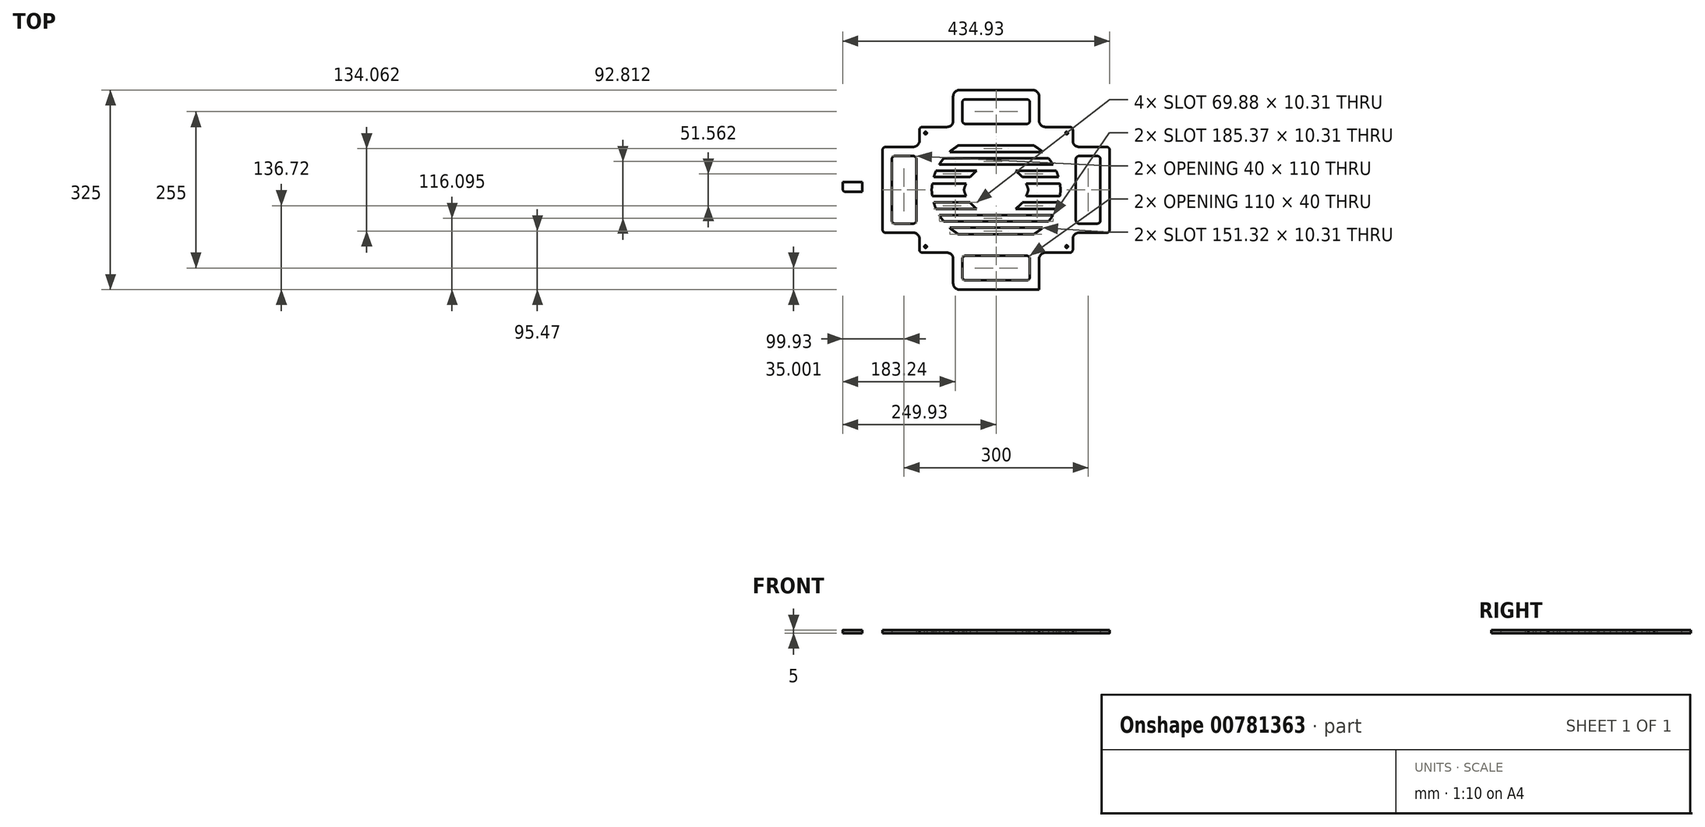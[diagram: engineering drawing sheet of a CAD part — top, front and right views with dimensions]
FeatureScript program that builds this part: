
annotation { "Feature Type Name" : "Feature", "Feature Type Description" : "" }
export const myFeature = defineFeature(function(context is Context, id is Id, definition is map)
    precondition{}
    {
        {
            var Q0;
            Q0=qCreatedBy(makeId("Top.planeOp"),FACE);
            var sketch = newSketch(context, id + "F0", { "sketchPlane" : qUnion([Q0])});
            skCircle(sketch, "E0", {"center": v(-230, 122.51) * mm, "radius": 2 * mm});
            skCircle(sketch, "E1", {"center": v(0, 122.51) * mm, "radius": 2 * mm});
            skCircle(sketch, "E2", {"center": v(0, -62.49) * mm, "radius": 2 * mm});
            skCircle(sketch, "E3", {"center": v(-230, -62.49) * mm, "radius": 2 * mm});
            skLineSegment(sketch, "E4.0", {"start": v(-230, 132.51) * mm, "end": v(-185, 132.51) * mm});
            skLineSegment(sketch, "E5.0", {"start": v(-240, 127.51) * mm, "end": v(-240, 110.01) * mm});
            skLineSegment(sketch, "E5.1", {"start": v(-235, 132.51) * mm, "end": v(-195, 132.51) * mm});
            skLineSegment(sketch, "E5.2", {"start": v(10, 127.51) * mm, "end": v(10, 110.01) * mm});
            skLineSegment(sketch, "E5.3", {"start": v(-235, -72.49) * mm, "end": v(-195, -72.49) * mm});
            skPoint(sketch, "E6.end.orphan", {"position": v(-290, 0) * mm});
            skLineSegment(sketch, "E7.bottom", {"start": v(-271.57, -39.99) * mm, "end": v(-290, -39.99) * mm});
            skPoint(sketch, "E8.end.orphan", {"position": v(-310, -39.99) * mm});
            skLineSegment(sketch, "E9", {"start": v(-290, 100.01) * mm, "end": v(-250, 100.01) * mm});
            skLineSegment(sketch, "E10", {"start": v(-290, -39.99) * mm, "end": v(-250, -39.99) * mm});
            skPoint(sketch, "E11.start.orphan", {"position": v(-240, 30.01) * mm});
            skLineSegment(sketch, "E12", {"start": v(-295, -39.99) * mm, "end": v(-290, -39.99) * mm});
            skLineSegment(sketch, "E13", {"start": v(-290, -39.99) * mm, "end": v(-295, -39.99) * mm});
            skLineSegment(sketch, "E14", {"start": v(-300, -34.99) * mm, "end": v(-300, 95.01) * mm});
            skLineSegment(sketch, "E15", {"start": v(-295, 100.01) * mm, "end": v(-290, 100.01) * mm});
            skPoint(sketch, "E16.visualSharp", {"position": v(-300, 100.01) * mm});
            skArc(sketch, "E16.filletArc", {"start": v(-295, 100.01) * mm, "mid": v(-298.54, 98.55) * mm, "end": v(-300, 95.01) * mm});
            skPoint(sketch, "E17.visualSharp", {"position": v(-300, -39.99) * mm});
            skArc(sketch, "E17.filletArc", {"start": v(-300, -34.99) * mm, "mid": v(-298.54, -38.52) * mm, "end": v(-295, -39.99) * mm});
            skLineSegment(sketch, "E18.0", {"start": v(-285, -19.99) * mm, "end": v(-285, 80.01) * mm});
            skLineSegment(sketch, "E19.0", {"start": v(-280, 85.01) * mm, "end": v(-250, 85.01) * mm});
            skLineSegment(sketch, "E20.0", {"start": v(-280, -24.99) * mm, "end": v(-250, -24.99) * mm});
            skPoint(sketch, "E21.visualSharp", {"position": v(-285, 85.01) * mm});
            skArc(sketch, "E21.filletArc", {"start": v(-280, 85.01) * mm, "mid": v(-283.54, 83.55) * mm, "end": v(-285, 80.01) * mm});
            skPoint(sketch, "E22.visualSharp", {"position": v(-285, -24.99) * mm});
            skArc(sketch, "E22.filletArc", {"start": v(-285, -19.99) * mm, "mid": v(-283.54, -23.52) * mm, "end": v(-280, -24.99) * mm});
            skLineSegment(sketch, "E23", {"start": v(-245, 68.7) * mm, "end": v(-245, 80.01) * mm});
            skLineSegment(sketch, "E24", {"start": v(-245, 80.01) * mm, "end": v(-245, -19.99) * mm});
            skArc(sketch, "E25.filletArc", {"start": v(-250, -24.99) * mm, "mid": v(-246.46, -23.52) * mm, "end": v(-245, -19.99) * mm});
            skArc(sketch, "E26.filletArc", {"start": v(-245, 80.01) * mm, "mid": v(-246.46, 83.55) * mm, "end": v(-250, 85.01) * mm});
            skLineSegment(sketch, "E27", {"start": v(-361.14, -2.55) * mm, "end": v(-350.49, -2.55) * mm});
            skLineSegment(sketch, "E28", {"start": v(-340.49, -12.55) * mm, "end": v(-340.49, -26.99) * mm});
            skPoint(sketch, "E29.visualSharp", {"position": v(-340.49, -2.55) * mm});
            skArc(sketch, "E29.filletArc", {"start": v(-340.49, -12.55) * mm, "mid": v(-343.42, -5.48) * mm, "end": v(-350.49, -2.55) * mm});
            skLineSegment(sketch, "E30", {"start": v(-240, -49.99) * mm, "end": v(-240, -67.49) * mm});
            skPoint(sketch, "E31.visualSharp", {"position": v(-240, -39.99) * mm});
            skArc(sketch, "E31.filletArc", {"start": v(-240, -49.99) * mm, "mid": v(-242.93, -42.92) * mm, "end": v(-250, -39.99) * mm});
            skLineSegment(sketch, "E32.bottom", {"start": v(-359.93, 26.54) * mm, "end": v(-333.44, 26.54) * mm});
            skLineSegment(sketch, "E32.top", {"start": v(-364.93, 42.53) * mm, "end": v(-333.44, 42.53) * mm});
            skLineSegment(sketch, "E32.left", {"start": v(-364.93, 31.54) * mm, "end": v(-364.93, 42.53) * mm});
            skLineSegment(sketch, "E32.right", {"start": v(-333.44, 26.54) * mm, "end": v(-333.44, 42.53) * mm});
            skPoint(sketch, "E33.visualSharp", {"position": v(-364.93, 26.54) * mm});
            skArc(sketch, "E33.filletArc", {"start": v(-364.93, 31.54) * mm, "mid": v(-363.46, 28) * mm, "end": v(-359.93, 26.54) * mm});
            skPoint(sketch, "E34.visualSharp", {"position": v(-240, -72.49) * mm});
            skArc(sketch, "E34.filletArc", {"start": v(-240, -67.49) * mm, "mid": v(-238.54, -71.02) * mm, "end": v(-235, -72.49) * mm});
            skPoint(sketch, "E35.visualSharp", {"position": v(-240, 132.51) * mm});
            skArc(sketch, "E35.filletArc", {"start": v(-235, 132.51) * mm, "mid": v(-238.54, 131.05) * mm, "end": v(-240, 127.51) * mm});
            skArc(sketch, "E36.MirrorCS", {"start": v(-240, 110.01) * mm, "mid": v(-242.93, 102.94) * mm, "end": v(-250, 100.01) * mm});
            skLineSegment(sketch, "E37.MirrorCS", {"start": v(65, -39.99) * mm, "end": v(60, -39.99) * mm});
            skArc(sketch, "E38.MirrorCS", {"start": v(70, -34.99) * mm, "mid": v(68.54, -38.52) * mm, "end": v(65, -39.99) * mm});
            skLineSegment(sketch, "E39.MirrorCS", {"start": v(10, -49.99) * mm, "end": v(10, -67.49) * mm});
            skLineSegment(sketch, "E40.MirrorCS", {"start": v(60, -39.99) * mm, "end": v(65, -39.99) * mm});
            skArc(sketch, "E41.MirrorCS", {"start": v(10, -67.49) * mm, "mid": v(8.54, -71.02) * mm, "end": v(5, -72.49) * mm});
            skArc(sketch, "E42.MirrorCS", {"start": v(5, 132.51) * mm, "mid": v(8.54, 131.05) * mm, "end": v(10, 127.51) * mm});
            skArc(sketch, "E43.MirrorCS", {"start": v(10, 110.01) * mm, "mid": v(12.93, 102.94) * mm, "end": v(20, 100.01) * mm});
            skArc(sketch, "E44.MirrorCS", {"start": v(20, -24.99) * mm, "mid": v(16.46, -23.52) * mm, "end": v(15, -19.99) * mm});
            skArc(sketch, "E45.MirrorCS", {"start": v(50, 85.01) * mm, "mid": v(53.54, 83.55) * mm, "end": v(55, 80.01) * mm});
            skArc(sketch, "E46.MirrorCS", {"start": v(55, -19.99) * mm, "mid": v(53.54, -23.52) * mm, "end": v(50, -24.99) * mm});
            skArc(sketch, "E47.MirrorCS", {"start": v(10, -49.99) * mm, "mid": v(12.93, -42.92) * mm, "end": v(20, -39.99) * mm});
            skLineSegment(sketch, "E48.MirrorCS", {"start": v(15, 68.7) * mm, "end": v(15, 80.01) * mm});
            skArc(sketch, "E49.MirrorCS", {"start": v(65, 100.01) * mm, "mid": v(68.54, 98.55) * mm, "end": v(70, 95.01) * mm});
            skArc(sketch, "E50.MirrorCS", {"start": v(15, 80.01) * mm, "mid": v(16.46, 83.55) * mm, "end": v(20, 85.01) * mm});
            skLineSegment(sketch, "E51.MirrorCS", {"start": v(65, 100.01) * mm, "end": v(60, 100.01) * mm});
            skPoint(sketch, "E52.MirrorP", {"position": v(70, -39.99) * mm});
            skLineSegment(sketch, "E53.MirrorCS", {"start": v(60, 100.01) * mm, "end": v(20, 100.01) * mm});
            skLineSegment(sketch, "E54.MirrorCS", {"start": v(50, 85.01) * mm, "end": v(20, 85.01) * mm});
            skLineSegment(sketch, "E55.MirrorCS", {"start": v(41.57, -39.99) * mm, "end": v(60, -39.99) * mm});
            skLineSegment(sketch, "E56.MirrorCS", {"start": v(60, -39.99) * mm, "end": v(20, -39.99) * mm});
            skPoint(sketch, "E57.MirrorP", {"position": v(70, 100.01) * mm});
            skLineSegment(sketch, "E58.MirrorCS", {"start": v(55, -19.99) * mm, "end": v(55, 80.01) * mm});
            skLineSegment(sketch, "E59.MirrorCS", {"start": v(15, 80.01) * mm, "end": v(15, -19.99) * mm});
            skLineSegment(sketch, "E60.MirrorCS", {"start": v(70, -34.99) * mm, "end": v(70, 95.01) * mm});
            skPoint(sketch, "E61.MirrorP", {"position": v(60, 0) * mm});
            skPoint(sketch, "E62.MirrorP", {"position": v(55, -24.99) * mm});
            skPoint(sketch, "E63.MirrorP", {"position": v(10, 132.51) * mm});
            skPoint(sketch, "E64.MirrorP", {"position": v(10, 30.01) * mm});
            skPoint(sketch, "E65.MirrorP", {"position": v(55, 85.01) * mm});
            skPoint(sketch, "E66.MirrorP", {"position": v(80, -39.99) * mm});
            skPoint(sketch, "E67.MirrorP", {"position": v(10, -39.99) * mm});
            skPoint(sketch, "E68.MirrorP", {"position": v(10, -72.49) * mm});
            skLineSegment(sketch, "E69", {"start": v(20, -24.99) * mm, "end": v(50, -24.99) * mm});
            skLineSegment(sketch, "E70", {"start": v(-235, -72.49) * mm, "end": v(-235, -67.49) * mm});
            skPoint(sketch, "E70.endSnap0", {"position": v(-220.07, 30.01) * mm});
            skLineSegment(sketch, "E71", {"start": v(-115, -132.49) * mm, "end": v(-185, -132.49) * mm});
            skLineSegment(sketch, "E72", {"start": v(-115, -132.49) * mm, "end": v(-45, -132.49) * mm});
            skLineSegment(sketch, "E73", {"start": v(-45, -122.49) * mm, "end": v(-45, -82.49) * mm});
            skLineSegment(sketch, "E74.bottom", {"start": v(-175, -132.49) * mm, "end": v(-55, -132.49) * mm});
            skLineSegment(sketch, "E74.left", {"start": v(-185, -122.49) * mm, "end": v(-185, -82.49) * mm});
            skLineSegment(sketch, "E74.right", {"start": v(-45, -132.49) * mm, "end": v(-45, -72.49) * mm});
            skLineSegment(sketch, "E75.0", {"start": v(-165, -117.49) * mm, "end": v(-65, -117.49) * mm});
            skLineSegment(sketch, "E76.0", {"start": v(-170, -112.49) * mm, "end": v(-170, -82.49) * mm});
            skLineSegment(sketch, "E77.0", {"start": v(-60, -112.49) * mm, "end": v(-60, -82.49) * mm});
            skLineSegment(sketch, "E78.0", {"start": v(-165, -77.49) * mm, "end": v(-65, -77.49) * mm});
            skLineSegment(sketch, "E79.trimOffspring", {"start": v(-35, -72.49) * mm, "end": v(5, -72.49) * mm});
            skPoint(sketch, "E80.visualSharp", {"position": v(-170, -117.49) * mm});
            skArc(sketch, "E80.filletArc", {"start": v(-170, -112.49) * mm, "mid": v(-168.54, -116.02) * mm, "end": v(-165, -117.49) * mm});
            skPoint(sketch, "E81.visualSharp", {"position": v(-170, -77.49) * mm});
            skArc(sketch, "E81.filletArc", {"start": v(-165, -77.49) * mm, "mid": v(-168.54, -78.95) * mm, "end": v(-170, -82.49) * mm});
            skPoint(sketch, "E82.visualSharp", {"position": v(-60, -77.49) * mm});
            skArc(sketch, "E82.filletArc", {"start": v(-60, -82.49) * mm, "mid": v(-61.46, -78.95) * mm, "end": v(-65, -77.49) * mm});
            skPoint(sketch, "E83.visualSharp", {"position": v(-60, -117.49) * mm});
            skArc(sketch, "E83.filletArc", {"start": v(-65, -117.49) * mm, "mid": v(-61.46, -116.02) * mm, "end": v(-60, -112.49) * mm});
            skPoint(sketch, "E84.visualSharp", {"position": v(-285.06, -102.44) * mm});
            skPoint(sketch, "E85.visualSharp", {"position": v(-185, -132.49) * mm});
            skArc(sketch, "E85.filletArc", {"start": v(-185, -122.49) * mm, "mid": v(-182.07, -129.56) * mm, "end": v(-175, -132.49) * mm});
            skPoint(sketch, "E86.visualSharp", {"position": v(-45, -132.49) * mm});
            skArc(sketch, "E86.filletArc", {"start": v(-55, -132.49) * mm, "mid": v(-47.93, -129.56) * mm, "end": v(-45, -122.49) * mm});
            skPoint(sketch, "E87.visualSharp", {"position": v(-185, -72.49) * mm});
            skArc(sketch, "E87.filletArc", {"start": v(-185, -82.49) * mm, "mid": v(-187.93, -75.42) * mm, "end": v(-195, -72.49) * mm});
            skPoint(sketch, "E88.visualSharp", {"position": v(-45, -72.49) * mm});
            skArc(sketch, "E88.filletArc", {"start": v(-35, -72.49) * mm, "mid": v(-42.07, -75.42) * mm, "end": v(-45, -82.49) * mm});
            skArc(sketch, "E89.MirrorCS", {"start": v(-35, 132.51) * mm, "mid": v(-42.07, 135.44) * mm, "end": v(-45, 142.51) * mm});
            skArc(sketch, "E90.MirrorCS", {"start": v(-170, 172.51) * mm, "mid": v(-168.54, 176.05) * mm, "end": v(-165, 177.51) * mm});
            skArc(sketch, "E91.MirrorCS", {"start": v(-240, 127.51) * mm, "mid": v(-238.54, 131.05) * mm, "end": v(-235, 132.51) * mm});
            skLineSegment(sketch, "E92.MirrorCS", {"start": v(10, 110.01) * mm, "end": v(10, 127.51) * mm});
            skArc(sketch, "E93.MirrorCS", {"start": v(-185, 182.51) * mm, "mid": v(-182.07, 189.58) * mm, "end": v(-175, 192.51) * mm});
            skArc(sketch, "E94.MirrorCS", {"start": v(-165, 137.51) * mm, "mid": v(-168.54, 138.98) * mm, "end": v(-170, 142.51) * mm});
            skArc(sketch, "E95.MirrorCS", {"start": v(-185, 142.51) * mm, "mid": v(-187.93, 135.44) * mm, "end": v(-195, 132.51) * mm});
            skArc(sketch, "E96.MirrorCS", {"start": v(-60, 142.51) * mm, "mid": v(-61.46, 138.98) * mm, "end": v(-65, 137.51) * mm});
            skArc(sketch, "E97.MirrorCS", {"start": v(-65, 177.51) * mm, "mid": v(-61.46, 176.05) * mm, "end": v(-60, 172.51) * mm});
            skArc(sketch, "E98.MirrorCS", {"start": v(-55, 192.51) * mm, "mid": v(-47.93, 189.58) * mm, "end": v(-45, 182.51) * mm});
            skLineSegment(sketch, "E99.MirrorCS", {"start": v(-45, 182.51) * mm, "end": v(-45, 142.51) * mm});
            skPoint(sketch, "E100.MirrorP", {"position": v(-60, 177.51) * mm});
            skLineSegment(sketch, "E101.MirrorCS", {"start": v(-115, 192.51) * mm, "end": v(-55, 192.51) * mm});
            skLineSegment(sketch, "E102.MirrorCS", {"start": v(-60, 172.51) * mm, "end": v(-60, 142.51) * mm});
            skLineSegment(sketch, "E103.MirrorCS", {"start": v(-170, 172.51) * mm, "end": v(-170, 142.51) * mm});
            skPoint(sketch, "E104.MirrorP", {"position": v(-170, 177.51) * mm});
            skLineSegment(sketch, "E105.MirrorCS", {"start": v(-185, 182.51) * mm, "end": v(-185, 142.51) * mm});
            skLineSegment(sketch, "E106.MirrorCS", {"start": v(-35, 132.51) * mm, "end": v(5, 132.51) * mm});
            skPoint(sketch, "E107.MirrorP", {"position": v(-60, 137.51) * mm});
            skLineSegment(sketch, "E108.MirrorCS", {"start": v(-165, 137.51) * mm, "end": v(-65, 137.51) * mm});
            skPoint(sketch, "E109.MirrorP", {"position": v(-45, 192.51) * mm});
            skLineSegment(sketch, "E110.MirrorCS", {"start": v(-165, 177.51) * mm, "end": v(-65, 177.51) * mm});
            skPoint(sketch, "E111.MirrorP", {"position": v(-185, 132.51) * mm});
            skPoint(sketch, "E112.MirrorP", {"position": v(-45, 132.51) * mm});
            skLineSegment(sketch, "E113.MirrorCS", {"start": v(-175, 192.51) * mm, "end": v(-55, 192.51) * mm});
            skPoint(sketch, "E114.MirrorP", {"position": v(-185, 192.51) * mm});
            skPoint(sketch, "E115.MirrorP", {"position": v(-170, 137.51) * mm});
            skLineSegment(sketch, "E116.trimOffspring", {"start": v(-35, 132.51) * mm, "end": v(0, 132.51) * mm});
            skPoint(sketch, "E117.end.orphan", {"position": v(-115, -72.49) * mm});
            skPoint(sketch, "E118.end.orphan", {"position": v(-115, 30.01) * mm});
            skPoint(sketch, "E119.orphan", {"position": v(-235, 30.01) * mm});
            skPoint(sketch, "E120.orphan", {"position": v(-200.13, 30.01) * mm});
            skPoint(sketch, "E121.end.orphan", {"position": v(-220, 110.01) * mm});
            skLineSegment(sketch, "E122", {"start": v(-115, -72.49) * mm, "end": v(-115, -52.49) * mm});
            skLineSegment(sketch, "E123.MirrorCS", {"start": v(-10, 112.51) * mm, "end": v(-10, 110.01) * mm});
            skLineSegment(sketch, "E124", {"start": v(-167.5, 112.51) * mm, "end": v(-114.87, 112.51) * mm});
            skLineSegment(sketch, "E125", {"start": v(-115, -52.49) * mm, "end": v(-114.87, -52.49) * mm});
            skPoint(sketch, "E126.start.orphan", {"position": v(-223.22, 112.51) * mm});
            skPoint(sketch, "E127.MirrorCS.end.orphan", {"position": v(-220, -52.49) * mm});
            skPoint(sketch, "E127.MirrorCS.start.orphan", {"position": v(-223.22, -52.49) * mm});
            skLineSegment(sketch, "E128", {"start": v(-207.68, -11.24) * mm, "end": v(-115, -11.24) * mm});
            skLineSegment(sketch, "E129.top", {"start": v(-207.68, -11.24) * mm, "end": v(-167.5, -11.24) * mm});
            skLineSegment(sketch, "E130.bottom", {"start": v(-216.63, 9.39) * mm, "end": v(-167.5, 9.39) * mm});
            skLineSegment(sketch, "E131", {"start": v(-220, 19.7) * mm, "end": v(-167.5, 19.7) * mm});
            skLineSegment(sketch, "E132.MirrorCS", {"start": v(-212.94, -0.93) * mm, "end": v(-167.5, -0.93) * mm});
            skPoint(sketch, "E133.MirrorP", {"position": v(-134.87, 30.01) * mm});
            skPoint(sketch, "E134.MirrorP", {"position": v(-114.93, 30.01) * mm});
            skLineSegment(sketch, "E135.MirrorCS", {"start": v(-163.85, 19.7) * mm, "end": v(-167.5, 19.7) * mm});
            skLineSegment(sketch, "E136.MirrorCS", {"start": v(-157.47, 9.39) * mm, "end": v(-167.5, 9.39) * mm});
            skLineSegment(sketch, "E137.MirrorCS", {"start": v(-146.75, -0.93) * mm, "end": v(-167.5, -0.93) * mm});
            skLineSegment(sketch, "E138", {"start": v(-190.66, -31.86) * mm, "end": v(-115, -31.86) * mm});
            skLineSegment(sketch, "E139", {"start": v(-200.5, -21.55) * mm, "end": v(-115, -21.55) * mm});
            skLineSegment(sketch, "E140", {"start": v(-176.47, -42.18) * mm, "end": v(-115, -42.18) * mm});
            skPoint(sketch, "E141.MirrorP", {"position": v(-220, 112.51) * mm});
            skLineSegment(sketch, "E142.MirrorCS", {"start": v(-220, 110.01) * mm, "end": v(-220, 112.51) * mm});
            skLineSegment(sketch, "E143.MirrorCS", {"start": v(-207.68, 71.26) * mm, "end": v(-167.5, 71.26) * mm});
            skLineSegment(sketch, "E144.MirrorCS", {"start": v(-176.47, 102.2) * mm, "end": v(-115, 102.2) * mm});
            skLineSegment(sketch, "E145.MirrorCS", {"start": v(-163.85, 40.32) * mm, "end": v(-167.5, 40.32) * mm});
            skLineSegment(sketch, "E146.MirrorCS", {"start": v(-212.94, 60.95) * mm, "end": v(-167.5, 60.95) * mm});
            skLineSegment(sketch, "E147.MirrorCS", {"start": v(-200.5, 81.57) * mm, "end": v(-115, 81.57) * mm});
            skLineSegment(sketch, "E148.MirrorCS", {"start": v(-207.68, 71.26) * mm, "end": v(-115, 71.26) * mm});
            skLineSegment(sketch, "E149.MirrorCS", {"start": v(-218.95, 40.32) * mm, "end": v(-167.5, 40.32) * mm});
            skLineSegment(sketch, "E150.MirrorCS", {"start": v(-190.66, 91.89) * mm, "end": v(-115, 91.89) * mm});
            skLineSegment(sketch, "E151.MirrorCS", {"start": v(-220, 112.51) * mm, "end": v(-115, 112.51) * mm});
            skLineSegment(sketch, "E152.MirrorCS", {"start": v(-146.75, 60.95) * mm, "end": v(-167.5, 60.95) * mm});
            skLineSegment(sketch, "E153.MirrorCS", {"start": v(-157.47, 50.64) * mm, "end": v(-167.5, 50.64) * mm});
            skLineSegment(sketch, "E154.MirrorCS", {"start": v(-216.63, 50.64) * mm, "end": v(-167.5, 50.64) * mm});
            skLineSegment(sketch, "E155", {"start": v(-220, 81.57) * mm, "end": v(-220, 91.89) * mm});
            skLineSegment(sketch, "E156", {"start": v(-220, 112.51) * mm, "end": v(-220, 102.2) * mm});
            skPoint(sketch, "E157.orphan", {"position": v(-167.5, 112.51) * mm});
            skPoint(sketch, "E158.trimOffspring.end.orphan", {"position": v(-167.5, 30.01) * mm});
            skPoint(sketch, "E159.start.orphan", {"position": v(-167.5, -52.49) * mm});
            skPoint(sketch, "E160.orphan", {"position": v(-115, -39.99) * mm});
            skPoint(sketch, "E161.MirrorCS.start.orphan", {"position": v(-115, 9.39) * mm});
            skLineSegment(sketch, "E162.trimOffspring", {"start": v(-115, 19.7) * mm, "end": v(-115, 9.39) * mm});
            skPoint(sketch, "E163.MirrorCS.start.orphan", {"position": v(-115, 50.64) * mm});
            skPoint(sketch, "E164.MirrorCS.end.orphan", {"position": v(-115, 60.95) * mm});
            skPoint(sketch, "E165.orphan", {"position": v(-220, 30.01) * mm});
            skLineSegment(sketch, "E166.MirrorCS", {"start": v(-10, 110.01) * mm, "end": v(-10, 112.51) * mm});
            skPoint(sketch, "E167.MirrorP", {"position": v(-10, -52.49) * mm});
            skPoint(sketch, "E168.MirrorP", {"position": v(-10, 112.51) * mm});
            skLineSegment(sketch, "E169.MirrorCS", {"start": v(-10, 112.51) * mm, "end": v(-10, 102.2) * mm});
            skLineSegment(sketch, "E170.MirrorCS", {"start": v(-22.32, -11.24) * mm, "end": v(-62.5, -11.24) * mm});
            skLineSegment(sketch, "E171.MirrorCS", {"start": v(-22.32, 71.26) * mm, "end": v(-62.5, 71.26) * mm});
            skPoint(sketch, "E172.MirrorP", {"position": v(-115.07, 30.01) * mm});
            skPoint(sketch, "E173.MirrorP", {"position": v(-10, 30.01) * mm});
            skLineSegment(sketch, "E174.MirrorCS", {"start": v(-66.15, 19.7) * mm, "end": v(-62.5, 19.7) * mm});
            skPoint(sketch, "E175.MirrorP", {"position": v(-9.93, 30.01) * mm});
            skLineSegment(sketch, "E176.MirrorCS", {"start": v(-72.53, 9.39) * mm, "end": v(-62.5, 9.39) * mm});
            skLineSegment(sketch, "E177.MirrorCS", {"start": v(-17.06, -0.93) * mm, "end": v(-62.5, -0.93) * mm});
            skLineSegment(sketch, "E178.MirrorCS", {"start": v(-39.34, 91.89) * mm, "end": v(-115, 91.89) * mm});
            skLineSegment(sketch, "E179.MirrorCS", {"start": v(-11.05, 19.7) * mm, "end": v(-62.5, 19.7) * mm});
            skLineSegment(sketch, "E180.MirrorCS", {"start": v(-11.05, 40.32) * mm, "end": v(-62.5, 40.32) * mm});
            skLineSegment(sketch, "E181.MirrorCS", {"start": v(-53.53, 102.2) * mm, "end": v(-115, 102.2) * mm});
            skLineSegment(sketch, "E182.MirrorCS", {"start": v(-72.53, 50.64) * mm, "end": v(-62.5, 50.64) * mm});
            skLineSegment(sketch, "E183.MirrorCS", {"start": v(-39.34, -31.86) * mm, "end": v(-115, -31.86) * mm});
            skPoint(sketch, "E184.MirrorP", {"position": v(-62.5, 112.51) * mm});
            skLineSegment(sketch, "E185.MirrorCS", {"start": v(-22.32, -11.24) * mm, "end": v(-115, -11.24) * mm});
            skLineSegment(sketch, "E186.MirrorCS", {"start": v(-13.37, 50.64) * mm, "end": v(-62.5, 50.64) * mm});
            skLineSegment(sketch, "E187.MirrorCS", {"start": v(-29.5, -21.55) * mm, "end": v(-115, -21.55) * mm});
            skLineSegment(sketch, "E188.MirrorCS", {"start": v(-83.25, -0.93) * mm, "end": v(-62.5, -0.93) * mm});
            skPoint(sketch, "E189.MirrorP", {"position": v(-62.5, -52.49) * mm});
            skLineSegment(sketch, "E190.MirrorCS", {"start": v(-29.5, 81.57) * mm, "end": v(-115, 81.57) * mm});
            skLineSegment(sketch, "E191.MirrorCS", {"start": v(-53.53, -42.18) * mm, "end": v(-115, -42.18) * mm});
            skLineSegment(sketch, "E192.MirrorCS", {"start": v(-13.37, 9.39) * mm, "end": v(-62.5, 9.39) * mm});
            skPoint(sketch, "E193.MirrorP", {"position": v(-95.13, 30.01) * mm});
            skPoint(sketch, "E194.MirrorP", {"position": v(-29.87, 30.01) * mm});
            skPoint(sketch, "E195.MirrorP", {"position": v(-62.5, 30.01) * mm});
            skPoint(sketch, "E196.MirrorP", {"position": v(-10, 110.01) * mm});
            skLineSegment(sketch, "E197.MirrorCS", {"start": v(-17.06, 60.95) * mm, "end": v(-62.5, 60.95) * mm});
            skLineSegment(sketch, "E198.MirrorCS", {"start": v(-83.25, 60.95) * mm, "end": v(-62.5, 60.95) * mm});
            skLineSegment(sketch, "E199.MirrorCS", {"start": v(-22.32, 71.26) * mm, "end": v(-115, 71.26) * mm});
            skPoint(sketch, "E200.trimOffspring.start.orphan", {"position": v(-115, -0.93) * mm});
            skArc(sketch, "E201", {"start": v(-115, -52.49) * mm, "mid": v(-114.93, -52.49) * mm, "end": v(-114.87, -52.49) * mm});
            skArc(sketch, "E202", {"start": v(-146.75, 60.95) * mm, "mid": v(-152.47, 56.16) * mm, "end": v(-157.47, 50.64) * mm});
            skArc(sketch, "E203.MirrorCS", {"start": v(-146.75, -0.93) * mm, "mid": v(-152.47, 3.86) * mm, "end": v(-157.47, 9.39) * mm});
            skArc(sketch, "E204.MirrorCS", {"start": v(-53.53, -42.18) * mm, "mid": v(-46.18, -37.37) * mm, "end": v(-39.34, -31.86) * mm});
            skArc(sketch, "E205.MirrorCS", {"start": v(-83.25, -0.93) * mm, "mid": v(-77.53, 3.86) * mm, "end": v(-72.53, 9.39) * mm});
            skArc(sketch, "E206.MirrorCS", {"start": v(-83.25, 60.95) * mm, "mid": v(-77.53, 56.16) * mm, "end": v(-72.53, 50.64) * mm});
            skArc(sketch, "E207.trimOffspring", {"start": v(-114.87, 112.51) * mm, "mid": v(-114.93, 112.51) * mm, "end": v(-115, 112.51) * mm});
            skPoint(sketch, "E208.orphan", {"position": v(-220, 71.26) * mm});
            skPoint(sketch, "E209.orphan", {"position": v(-115, 40.32) * mm});
            skArc(sketch, "E210.trimOffspring", {"start": v(-163.85, 40.32) * mm, "mid": v(-165.94, 35.26) * mm, "end": v(-167.5, 30.01) * mm});
            skArc(sketch, "E211.trimOffspring", {"start": v(-218.95, 40.32) * mm, "mid": v(-219.62, 35.18) * mm, "end": v(-220, 30.01) * mm});
            skPoint(sketch, "E212.orphan", {"position": v(-220, 50.64) * mm});
            skPoint(sketch, "E213.end.orphan", {"position": v(-220, 60.95) * mm});
            skPoint(sketch, "E214.orphan", {"position": v(-220, 40.32) * mm});
            skArc(sketch, "E215.trimOffspring", {"start": v(-212.94, 60.95) * mm, "mid": v(-214.95, 55.85) * mm, "end": v(-216.63, 50.64) * mm});
            skArc(sketch, "E216.trimOffspring", {"start": v(-200.5, 81.57) * mm, "mid": v(-204.27, 76.55) * mm, "end": v(-207.68, 71.26) * mm});
            skArc(sketch, "E217.trimOffspring", {"start": v(-29.5, 81.57) * mm, "mid": v(-19.89, 66.91) * mm, "end": v(-13.37, 50.64) * mm});
            skArc(sketch, "E218.trimOffspring", {"start": v(-53.53, 102.2) * mm, "mid": v(-46.18, 97.4) * mm, "end": v(-39.34, 91.89) * mm});
            skArc(sketch, "E219.trimOffspring", {"start": v(-176.47, 102.2) * mm, "mid": v(-183.82, 97.4) * mm, "end": v(-190.66, 91.89) * mm});
            skLineSegment(sketch, "E220.trimOffspring", {"start": v(-114.87, 112.51) * mm, "end": v(-115, 112.51) * mm});
            skLineSegment(sketch, "E221.trimOffspring", {"start": v(-62.5, 112.51) * mm, "end": v(-10, 112.51) * mm});
            skPoint(sketch, "E222.orphan", {"position": v(-10, 71.26) * mm});
            skPoint(sketch, "E223.MirrorCS.end.orphan", {"position": v(-10, 91.89) * mm});
            skPoint(sketch, "E223.MirrorCS.start.orphan", {"position": v(-10, 81.57) * mm});
            skPoint(sketch, "E224.orphan", {"position": v(-115, 19.7) * mm});
            skPoint(sketch, "E225.MirrorCS.end.orphan", {"position": v(-62.5, 40.32) * mm});
            skArc(sketch, "E226.trimOffspring", {"start": v(-163.85, 19.7) * mm, "mid": v(-165.94, 24.76) * mm, "end": v(-167.5, 30.01) * mm});
            skPoint(sketch, "E227.orphan", {"position": v(-115, -11.24) * mm});
            skPoint(sketch, "E228.orphan", {"position": v(-115, 71.26) * mm});
            skLineSegment(sketch, "E229", {"start": v(-62.5, 40.32) * mm, "end": v(-66.15, 40.32) * mm});
            skArc(sketch, "E230.trimOffspring", {"start": v(-66.15, 40.32) * mm, "mid": v(-64.06, 35.26) * mm, "end": v(-62.5, 30.01) * mm});
            skArc(sketch, "E231.trimOffspring", {"start": v(-66.15, 19.7) * mm, "mid": v(-64.06, 24.76) * mm, "end": v(-62.5, 30.01) * mm});
            skPoint(sketch, "E232.orphan", {"position": v(-10, -11.24) * mm});
            skPoint(sketch, "E233.orphan", {"position": v(-220, -42.18) * mm});
            skPoint(sketch, "E234.orphan", {"position": v(-220, -31.86) * mm});
            skPoint(sketch, "E235.orphan", {"position": v(-220, -21.55) * mm});
            skPoint(sketch, "E236.orphan", {"position": v(-220, -11.24) * mm});
            skPoint(sketch, "E237.orphan", {"position": v(-220, -0.93) * mm});
            skPoint(sketch, "E238.orphan", {"position": v(-220, 9.39) * mm});
            skArc(sketch, "E239.trimOffspring", {"start": v(-218.95, 19.7) * mm, "mid": v(-219.62, 24.84) * mm, "end": v(-220, 30.01) * mm});
            skArc(sketch, "E240.trimOffspring", {"start": v(-212.94, -0.93) * mm, "mid": v(-214.95, 4.17) * mm, "end": v(-216.63, 9.39) * mm});
            skArc(sketch, "E241.trimOffspring", {"start": v(-200.5, -21.55) * mm, "mid": v(-204.27, -16.52) * mm, "end": v(-207.68, -11.24) * mm});
            skArc(sketch, "E242.trimOffspring", {"start": v(-176.47, -42.18) * mm, "mid": v(-183.82, -37.37) * mm, "end": v(-190.66, -31.86) * mm});
            skLineSegment(sketch, "E243.trimOffspring", {"start": v(-114.87, -52.49) * mm, "end": v(-115, -52.49) * mm});
            skPoint(sketch, "E244.orphan", {"position": v(-115, -52.49) * mm});
            skArc(sketch, "E245.trimOffspring", {"start": v(-29.5, -21.55) * mm, "mid": v(-25.73, -16.52) * mm, "end": v(-22.32, -11.24) * mm});
            skArc(sketch, "E246.trimOffspring", {"start": v(-17.06, -0.93) * mm, "mid": v(-15.05, 4.17) * mm, "end": v(-13.37, 9.39) * mm});
            skArc(sketch, "E247.trimOffspring", {"start": v(-11.05, 19.7) * mm, "mid": v(-10.38, 24.84) * mm, "end": v(-10, 30.01) * mm});
            skArc(sketch, "E248.trimOffspring", {"start": v(-11.05, 40.32) * mm, "mid": v(-10.38, 35.18) * mm, "end": v(-10, 30.01) * mm});
            skPoint(sketch, "E249.orphan", {"position": v(-10, 60.95) * mm});
            skPoint(sketch, "E250.trimOffspring.start.orphan", {"position": v(-10, 50.64) * mm});
            skPoint(sketch, "E251.orphan", {"position": v(-10, 40.32) * mm});
            skPoint(sketch, "E252.orphan", {"position": v(-10, 9.39) * mm});
            skPoint(sketch, "E253.orphan", {"position": v(-10, 19.7) * mm});
            skPoint(sketch, "E254.trimOffspring.start.orphan", {"position": v(-10, -42.18) * mm});
            skPoint(sketch, "E255.MirrorCS.start.orphan", {"position": v(-10, -31.86) * mm});
            skPoint(sketch, "E256.orphan", {"position": v(-10, -21.55) * mm});
            skPoint(sketch, "E257.MirrorCS.end.orphan", {"position": v(-10, -0.93) * mm});
            skSolve(sketch);
        }
        {
            var Q0;
            Q0 = qSketchRegion(id + "F0", true);
            var Q1;
            Q1=makeQuery(id+"F0.imprint","IMPRINT",FACE,{"disambiguationData":[TD([[makeQuery(id+"F0.imprint","IMPRINT",EDGE,{"derivedFrom":sQuery(id+"F0.wireOp",EDGE,"E0")}),-1.0]])]});
            extrude(context, id + "F1", {"entities" : qUnion([Q0, Q1]), "depth" : 5 * mm, "offsetDistance" : 25 * mm});
        }
    });
